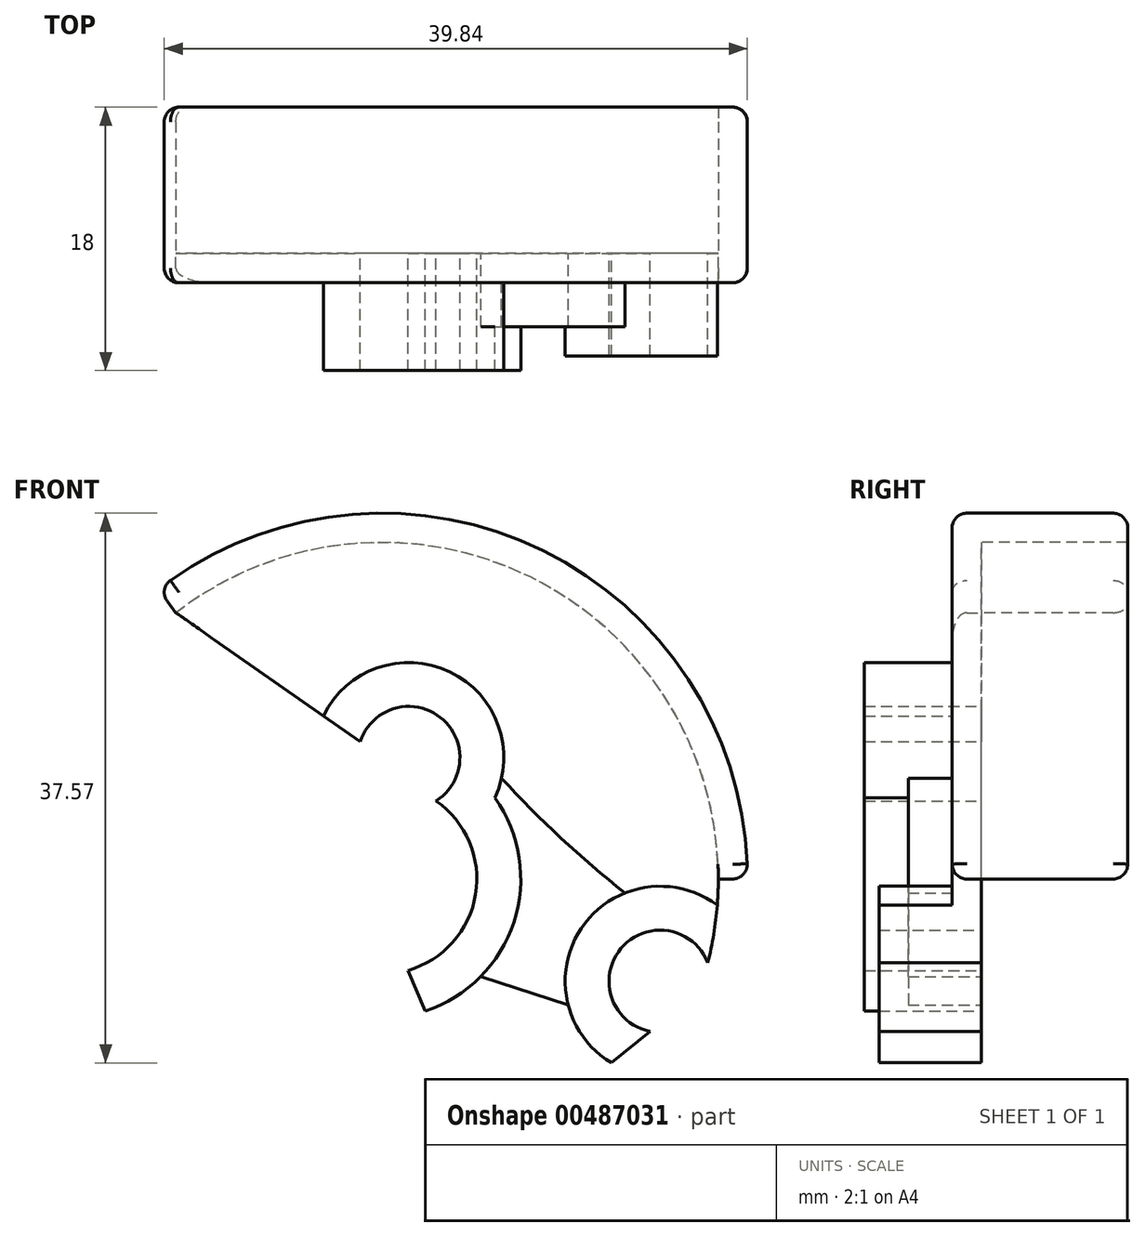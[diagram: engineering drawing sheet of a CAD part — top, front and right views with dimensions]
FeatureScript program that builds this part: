
annotation { "Feature Type Name" : "Feature", "Feature Type Description" : "" }
export const myFeature = defineFeature(function(context is Context, id is Id, definition is map)
    precondition{}
    {
        {
            var Q0;
            Q0=qCreatedBy(makeId("Front.planeOp"),FACE);
            var sketch = newSketch(context, id + "F0", { "sketchPlane" : qUnion([Q0])});
            skCircle(sketch, "E0", {"center": v(0, 0) * mm, "radius": 5.4 * mm});
            skCircle(sketch, "E1", {"center": v(0, 0) * mm, "radius": 6.5 * mm});
            skPoint(sketch, "E2", {"position": v(1.84, 8.3) * mm});
            skPoint(sketch, "E3", {"position": v(19.03, -7) * mm});
            skPoint(sketch, "E4", {"position": v(-1.97, -8.78) * mm});
            skCircle(sketch, "E5", {"center": v(1.84, 8.3) * mm, "radius": 3.5 * mm});
            skCircle(sketch, "E6", {"center": v(-1.97, -8.78) * mm, "radius": 3.5 * mm});
            skCircle(sketch, "E7", {"center": v(19.03, -7) * mm, "radius": 3.5 * mm});
            skArc(sketch, "E8", {"start": v(8.18, 6.89) * mm, "mid": v(12.25, 2.8) * mm, "end": v(16.63, -0.96) * mm});
            skArc(sketch, "E9", {"start": v(22.28, -5.72) * mm, "mid": v(12.64, 19.21) * mm, "end": v(-14.07, 18.2) * mm});
            skArc(sketch, "E10", {"start": v(25, 0) * mm, "mid": v(11.03, 22.44) * mm, "end": v(-15.27, 19.8) * mm});
            skLineSegment(sketch, "E11", {"start": v(-15.27, 19.8) * mm, "end": v(-14.07, 18.2) * mm});
            skFitSpline(sketch, "E12", {"points": [v(23, 0) * mm, v(25, 0) * mm], "startDerivative": vector(2, 0) * mm, "endDerivative": vector(2, 0) * mm});
            skArc(sketch, "E13", {"start": v(2.97, -9.02) * mm, "mid": v(9.03, -2.95) * mm, "end": v(7.72, 5.53) * mm});
            skArc(sketch, "E14", {"start": v(22.93, -1.8) * mm, "mid": v(13.64, -3.37) * mm, "end": v(15.69, -12.57) * mm});
            skLineSegment(sketch, "E15", {"start": v(-14.07, 18.2) * mm, "end": v(-1.48, 9.38) * mm});
            skArc(sketch, "E16.trimOffspring", {"start": v(7.72, 5.53) * mm, "mid": v(4.65, 14.16) * mm, "end": v(-4, 11.15) * mm});
            skLineSegment(sketch, "E17", {"start": v(6.77, -6.67) * mm, "end": v(12.74, -8.62) * mm});
            skLineSegment(sketch, "E18", {"start": v(18.33, -10.42) * mm, "end": v(15.69, -12.57) * mm});
            skLineSegment(sketch, "E19", {"start": v(1.79, -6.25) * mm, "end": v(2.97, -9.02) * mm});
            skSolve(sketch);
        }
        {
            var Q0;
            Q0=makeQuery(id+"F0.imprint","IMPRINT",FACE,{"disambiguationData":[TD([[makeQuery(id+"F0.imprint","IMPRINT",EDGE,{"derivedFrom":sQuery(id+"F0.wireOp",EDGE,"E10")}),1.0]])]});
            extrude(context, id + "F1", {"entities" : qUnion([Q0]), "oppositeDirection" : true, "depth" : 10 * mm});
        }
        {
            var Q0;
            {var subQ1=sQuery(id+"F0.wireOp",EDGE,"E8");Q0=makeQuery(id+"F0.imprint","IMPRINT",FACE,{"disambiguationData":[TD([[makeQuery(id+"F0.imprint","IMPRINT",EDGE,{"derivedFrom":subQ1}),1.0]])]});}
            var Q1;
            Q1=makeQuery(id+"F0.imprint","IMPRINT",FACE,{"disambiguationData":[TD([[makeQuery(id+"F0.imprint","IMPRINT",EDGE,{"derivedFrom":sQuery(id+"F0.wireOp",EDGE,"E10")}),1.0]])]});
            extrude(context, id + "F2", {"entities" : qUnion([Q0, Q1]), "operationType" : NewBodyOperationType.ADD, "depth" : 2 * mm});
        }
        {
            var Q0;
            Q0=makeQuery(id+"F2.opExtrude","CAP_EDGE",EDGE,{"disambiguationData":[OSD([sQuery(id+"F0.wireOp",EDGE,"E10")])],"isStart":false});
            var Q1;
            Q1=makeQuery(id+"F1.opExtrude","CAP_EDGE",EDGE,{"disambiguationData":[OSD([sQuery(id+"F0.wireOp",EDGE,"E10")])],"isStart":false});
            fillet(context, id + "F3", {"entities" : qUnion([Q0, Q1]), "radius" : 1 * mm, "tangentPropagation" : true, "allowEdgeOverflow" : false});
        }
        {
            var Q0;
            {var subQ0=sQuery(id+"F0.wireOp",EDGE,"E12");var subQ1=sQuery(id+"F0.wireOp",EDGE,"E10");Q0=makeQuery(id+"F2.boolean.opBoolean","MERGE",EDGE,{"derivedFrom":[makeQuery(id+"F1.opExtrude","SWEPT_EDGE",EDGE,{"disambiguationData":[OSD([subQ1,subQ0])]}),makeQuery(id+"F2.opExtrude","SWEPT_EDGE",EDGE,{"disambiguationData":[OSD([subQ1,subQ0])]})]});}
            fillet(context, id + "F4", {"entities" : qUnion([Q0]), "radius" : 1 * mm, "tangentPropagation" : true, "allowEdgeOverflow" : false});
        }
        {
            var Q0;
            {var subQ4=sQuery(id+"F0.wireOp",EDGE,"E19");Q0=makeQuery(id+"F0.imprint","IMPRINT",FACE,{"disambiguationData":[TD([[makeQuery(id+"F0.imprint","IMPRINT",EDGE,{"derivedFrom":subQ4}),1.0]])]});}
            extrude(context, id + "F5", {"entities" : qUnion([Q0]), "operationType" : NewBodyOperationType.ADD, "depth" : 8 * mm});
        }
        {
            var Q0;
            {var subQ7=sQuery(id+"F0.wireOp",EDGE,"E18");Q0=makeQuery(id+"F0.imprint","IMPRINT",FACE,{"disambiguationData":[TD([[makeQuery(id+"F0.imprint","IMPRINT",EDGE,{"derivedFrom":subQ7}),-1.0]])]});}
            extrude(context, id + "F6", {"entities" : qUnion([Q0]), "operationType" : NewBodyOperationType.ADD, "depth" : 7 * mm});
        }
        {
            var Q0;
            {var subQ1=sQuery(id+"F0.wireOp",EDGE,"E8");Q0=makeQuery(id+"F0.imprint","IMPRINT",FACE,{"disambiguationData":[TD([[makeQuery(id+"F0.imprint","IMPRINT",EDGE,{"derivedFrom":subQ1}),-1.0]])]});}
            extrude(context, id + "F7", {"entities" : qUnion([Q0]), "operationType" : NewBodyOperationType.ADD, "depth" : 5 * mm});
        }
        {
            var Q0;
            {var subQ0=sQuery(id+"F0.wireOp",EDGE,"E11");var subQ1=sQuery(id+"F0.wireOp",EDGE,"E10");Q0=makeQuery(id+"F2.boolean.opBoolean","MERGE",EDGE,{"derivedFrom":[makeQuery(id+"F1.opExtrude","SWEPT_EDGE",EDGE,{"disambiguationData":[OSD([subQ1,subQ0])]}),makeQuery(id+"F2.opExtrude","SWEPT_EDGE",EDGE,{"disambiguationData":[OSD([subQ1,subQ0])]})]});}
            fillet(context, id + "F8", {"entities" : qUnion([Q0]), "radius" : 1 * mm, "tangentPropagation" : true, "allowEdgeOverflow" : false});
        }
    });
